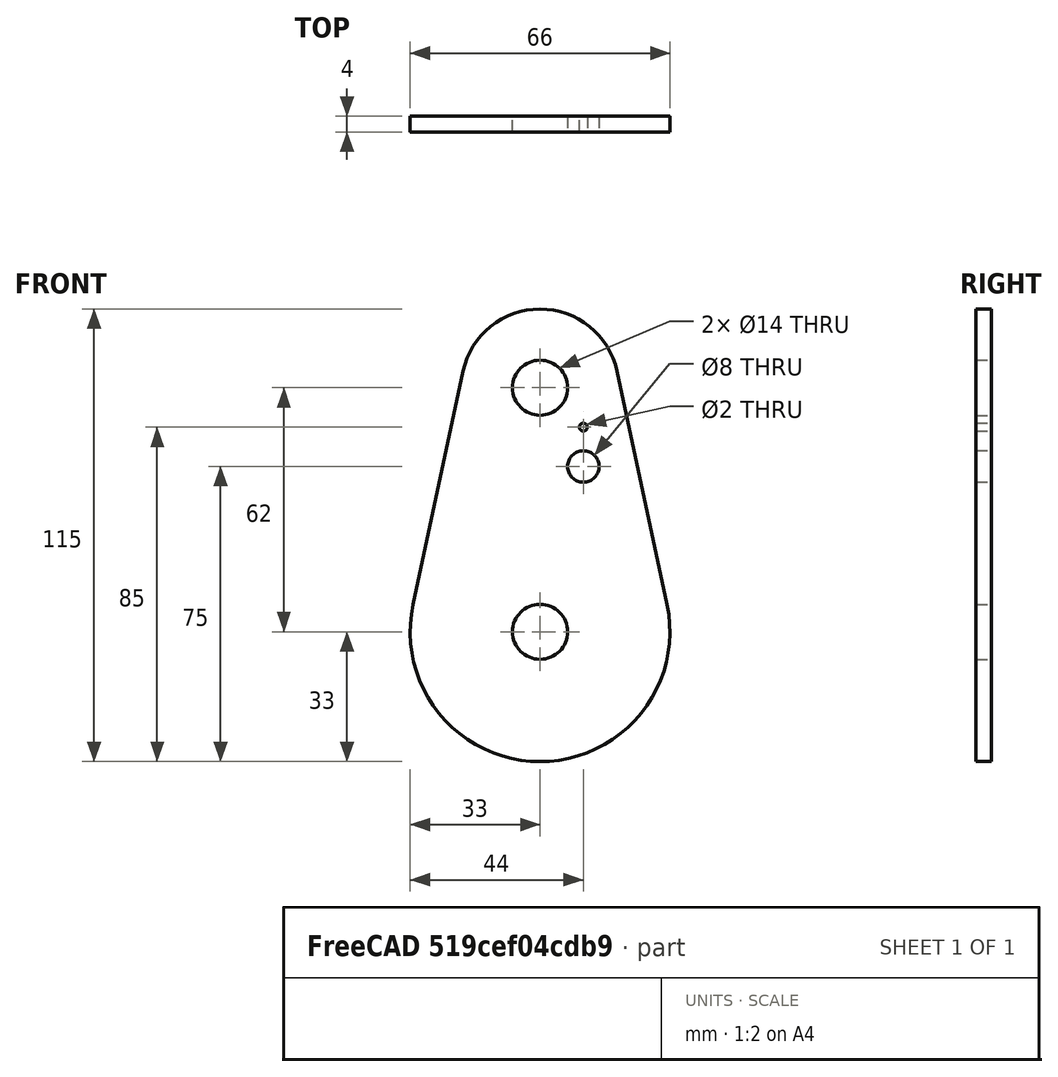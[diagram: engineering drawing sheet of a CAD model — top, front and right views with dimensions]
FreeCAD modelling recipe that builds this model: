
FCSTD DOCUMENT  (FreeCAD 0.16RUnknown)
Label: placa base
License: All rights reserved
LicenseURL: http://en.wikipedia.org/wiki/All_rights_reserved
objects: Sketcher::SketchObject×1, PartDesign::Pad×1
note: 3 computed .brp shape members not serialized (recipe doc carries the construction recipe); baked Part::Feature solids carry a one-line shape summary decoded from their .brp

FEATURE [Sketcher::SketchObject] Sketch
  Placement = pos=(0,0,0) rot=(-1,0,0;4.71239rad)
  sketch-geometry (8):
    g0: LineSegment StartX=-19.5554 StartY=66.1935 StartZ=0 EndX=-32.2664 EndY=6.91936 EndZ=0
    g1: LineSegment StartX=19.5554 StartY=66.1936 StartZ=0 EndX=32.2664 EndY=6.91936 EndZ=0
    g2: ArcOfCircle CenterX=0 CenterY=62 CenterZ=0 NormalX=0 NormalY=0 NormalZ=1 Radius=20 StartAngle=0.211248 EndAngle=2.93035
    g3: ArcOfCircle CenterX=0 CenterY=0 CenterZ=0 NormalX=0 NormalY=0 NormalZ=1 Radius=33 StartAngle=2.93035 EndAngle=6.49443
    g4: Circle CenterX=0 CenterY=62 CenterZ=0 NormalX=0 NormalY=0 NormalZ=1 Radius=7
    g5: Circle CenterX=0 CenterY=0 CenterZ=0 NormalX=0 NormalY=0 NormalZ=1 Radius=7
    g6: Circle CenterX=11 CenterY=42 CenterZ=0 NormalX=0 NormalY=0 NormalZ=1 Radius=4
    g7: Circle CenterX=11 CenterY=52 CenterZ=0 NormalX=0 NormalY=0 NormalZ=1 Radius=1
  constraints (23):
    c: Coincident(g2,g0)
    c: Coincident(g2,g1)
    c: Coincident(g3,g-1)
    c: Coincident(g3,g0)
    c: Coincident(g3,g1)
    c: DistanceY(g-1,g2) = 62
    c: Tangent(g2,g1)
    c: Tangent(g0,g2)
    c: Tangent(g3,g0)
    c: Tangent(g3,g1)
    c: Radius(g3) = 33
    c: Radius(g2) = 20
    c: PointOnObject(g2,g-2)
    c: Coincident(g4,g2)
    c: Coincident(g5,g-1)
    c: Radius(g5) = 7
    c: Equal(g5,g4)
    c: Radius(g6) = 4
    c: DistanceX(g2,g6) = 11
    c: DistanceY(g6,g2) = 20
    c: Radius(g7) = 1
    c: DistanceY(g6,g7) = 10
    c: DistanceX(g2,g7) = 11
FEATURE [PartDesign::Pad] Pad
  Length = 4
  Length2 = 100
  Placement = pos=(0,0,0) rot=(-1,0,0;4.71239rad)
  Sketch = -> Sketch
  Type = 0
